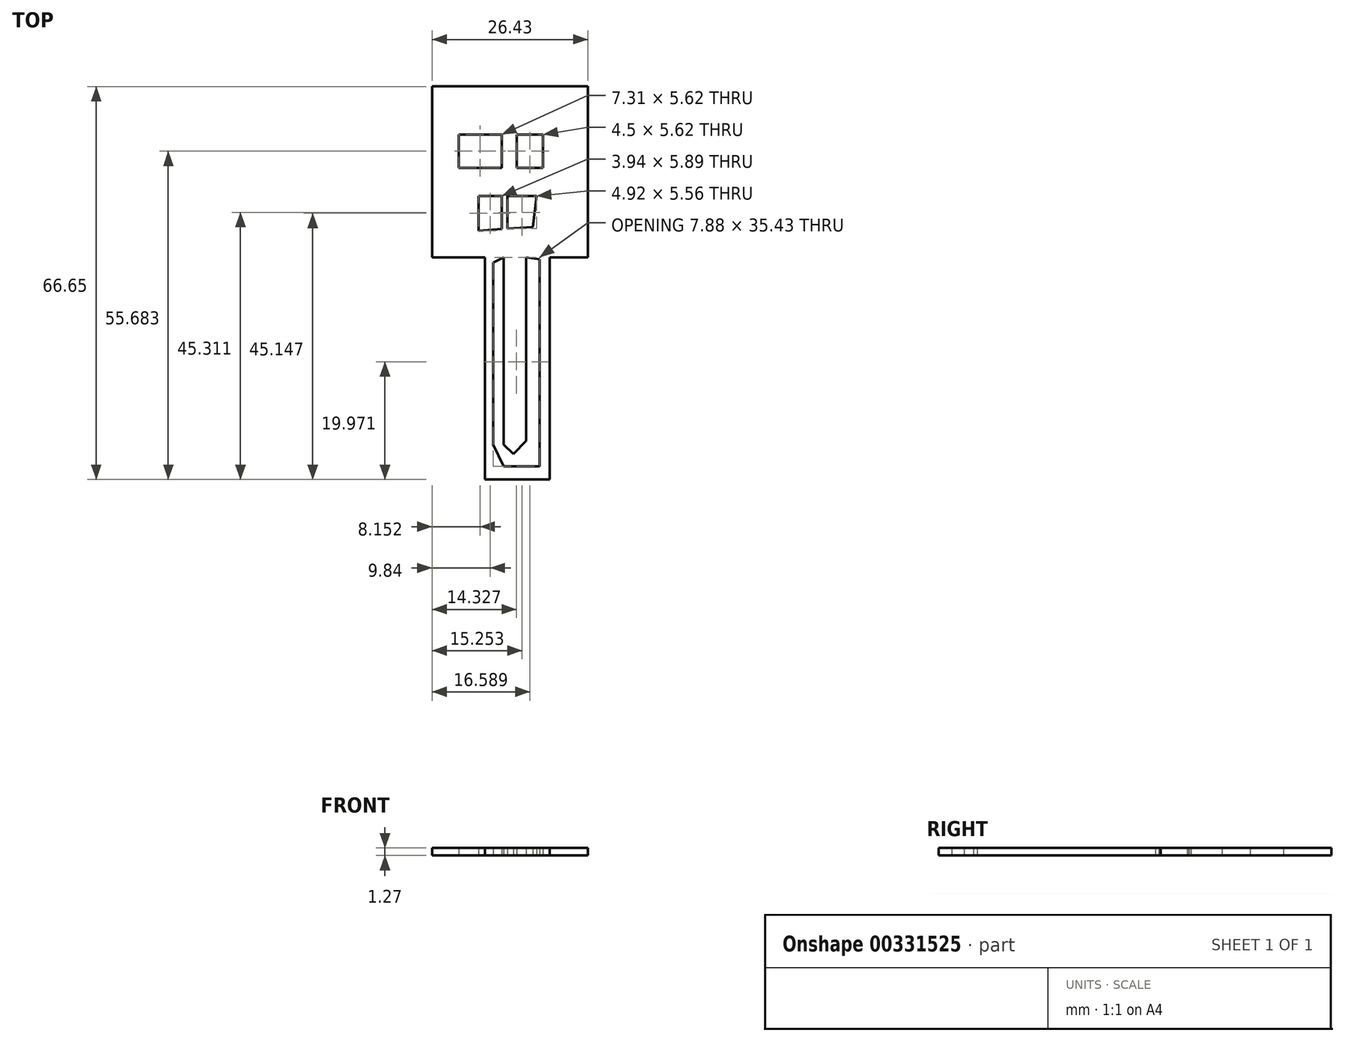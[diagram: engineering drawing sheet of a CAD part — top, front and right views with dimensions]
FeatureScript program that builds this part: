
annotation { "Feature Type Name" : "Feature", "Feature Type Description" : "" }
export const myFeature = defineFeature(function(context is Context, id is Id, definition is map)
    precondition{}
    {
        {
            var Q0;
            Q0=qCreatedBy(makeId("Top.planeOp"),FACE);
            var sketch = newSketch(context, id + "F0", { "sketchPlane" : qUnion([Q0])});
            skLineSegment(sketch, "E0", {"start": v(-60.18, 43.73) * mm, "end": v(-60.18, 14.76) * mm});
            skLineSegment(sketch, "E1", {"start": v(-60.18, 43.73) * mm, "end": v(-33.75, 43.73) * mm});
            skLineSegment(sketch, "E2", {"start": v(-33.75, 43.73) * mm, "end": v(-33.75, 14.76) * mm});
            skLineSegment(sketch, "E3", {"start": v(-33.75, 14.76) * mm, "end": v(-40.22, 14.76) * mm});
            skLineSegment(sketch, "E4", {"start": v(-40.22, 14.76) * mm, "end": v(-40.22, -22.92) * mm});
            skLineSegment(sketch, "E5", {"start": v(-40.22, -22.92) * mm, "end": v(-51.18, -22.92) * mm});
            skLineSegment(sketch, "E6", {"start": v(-51.18, -22.92) * mm, "end": v(-51.18, 14.76) * mm});
            skLineSegment(sketch, "E7", {"start": v(-52.03, 43.73) * mm, "end": v(-52.03, 38.1) * mm});
            skLineSegment(sketch, "E8", {"start": v(-44.72, 43.73) * mm, "end": v(-44.72, 38.1) * mm});
            skLineSegment(sketch, "E9.bottom", {"start": v(-48.37, 29.95) * mm, "end": v(-55.68, 29.95) * mm});
            skLineSegment(sketch, "E9.top", {"start": v(-48.37, 35.58) * mm, "end": v(-55.68, 35.58) * mm});
            skLineSegment(sketch, "E9.left", {"start": v(-48.37, 29.95) * mm, "end": v(-48.37, 35.58) * mm});
            skLineSegment(sketch, "E9.right", {"start": v(-55.68, 29.95) * mm, "end": v(-55.68, 35.58) * mm});
            skPoint(sketch, "E9.middle", {"position": v(-52.03, 32.76) * mm});
            skPoint(sketch, "E9.cornerSnap0", {"position": v(-48.37, 36.42) * mm});
            skLineSegment(sketch, "E10.bottom", {"start": v(-45.84, 29.95) * mm, "end": v(-41.34, 29.95) * mm});
            skLineSegment(sketch, "E10.top", {"start": v(-45.84, 35.58) * mm, "end": v(-41.34, 35.58) * mm});
            skLineSegment(sketch, "E10.left", {"start": v(-45.84, 29.95) * mm, "end": v(-45.84, 35.58) * mm});
            skLineSegment(sketch, "E10.right", {"start": v(-41.34, 29.95) * mm, "end": v(-41.34, 35.58) * mm});
            skPoint(sketch, "E10.middle", {"position": v(-43.6, 32.76) * mm});
            skLineSegment(sketch, "E11", {"start": v(-52.3, 25.17) * mm, "end": v(-52.3, 19.28) * mm});
            skLineSegment(sketch, "E12", {"start": v(-52.3, 19.28) * mm, "end": v(-48.37, 19.55) * mm});
            skLineSegment(sketch, "E13", {"start": v(-52.3, 25.17) * mm, "end": v(-48.37, 25.17) * mm});
            skLineSegment(sketch, "E14", {"start": v(-48.05, 14.76) * mm, "end": v(-48.05, -17.01) * mm});
            skPoint(sketch, "E15.endSnap0", {"position": v(-45.7, -22.92) * mm});
            skLineSegment(sketch, "E16", {"start": v(-41.91, -17.23) * mm, "end": v(-41.63, -17.01) * mm});
            skLineSegment(sketch, "E17", {"start": v(-45.47, 36.42) * mm, "end": v(-45.84, 35.58) * mm});
            skLineSegment(sketch, "E18", {"start": v(-60.18, 14.76) * mm, "end": v(-51.18, 14.76) * mm});
            skLineSegment(sketch, "E19", {"start": v(-42.47, 25.17) * mm, "end": v(-43.09, 19.9) * mm});
            skPoint(sketch, "E20.start.orphan", {"position": v(-47.39, 25.17) * mm});
            skLineSegment(sketch, "E21", {"start": v(-44.72, 38.1) * mm, "end": v(-45.47, 36.42) * mm});
            skPoint(sketch, "E22.startSnap0", {"position": v(-43.6, 35.58) * mm});
            skPoint(sketch, "E22.endSnap0", {"position": v(-48.37, 32.76) * mm});
            skLineSegment(sketch, "E23", {"start": v(-49.8, 13.87) * mm, "end": v(-49.8, 1.66) * mm});
            skLineSegment(sketch, "E24", {"start": v(-49.8, 1.66) * mm, "end": v(-49.8, -10.1) * mm});
            skLineSegment(sketch, "E25", {"start": v(-49.8, -10.1) * mm, "end": v(-49.8, -17.01) * mm});
            skLineSegment(sketch, "E26", {"start": v(-49.8, -17.01) * mm, "end": v(-48.05, -20.66) * mm});
            skLineSegment(sketch, "E27", {"start": v(-48.05, -20.66) * mm, "end": v(-45.7, -20.66) * mm});
            skLineSegment(sketch, "E28", {"start": v(-45.7, -20.66) * mm, "end": v(-41.91, -20.66) * mm});
            skLineSegment(sketch, "E29", {"start": v(-41.91, -20.66) * mm, "end": v(-41.91, -11.02) * mm});
            skLineSegment(sketch, "E30", {"start": v(-41.91, -11.02) * mm, "end": v(-41.91, -2.64) * mm});
            skLineSegment(sketch, "E31", {"start": v(-41.91, -2.64) * mm, "end": v(-41.91, 5.39) * mm});
            skLineSegment(sketch, "E32", {"start": v(-41.91, 5.39) * mm, "end": v(-41.91, 14.46) * mm});
            skPoint(sketch, "E33.start.orphan", {"position": v(-48.37, 19.55) * mm});
            skLineSegment(sketch, "E34", {"start": v(-49.8, 13.87) * mm, "end": v(-48.05, 14.76) * mm});
            skLineSegment(sketch, "E35", {"start": v(-41.91, 14.46) * mm, "end": v(-40.22, 14.76) * mm});
            skPoint(sketch, "E36.start.orphan", {"position": v(-56.8, 36.42) * mm});
            skPoint(sketch, "E37.startSnap0", {"position": v(-36.98, 14.76) * mm});
            skPoint(sketch, "E37.start.orphan", {"position": v(-36.98, 17.85) * mm});
            skPoint(sketch, "E38.trimOffspring.end.orphan", {"position": v(-39.93, 36.42) * mm});
            skLineSegment(sketch, "E39", {"start": v(-52.03, 38.1) * mm, "end": v(-48.37, 35.58) * mm});
            skPoint(sketch, "E40.start.orphan", {"position": v(-42.75, 14.76) * mm});
            skPoint(sketch, "E15.end.orphan", {"position": v(-45.7, -20.1) * mm});
            skLineSegment(sketch, "E41", {"start": v(-48.05, -17.01) * mm, "end": v(-46.4, -18.6) * mm});
            skLineSegment(sketch, "E42", {"start": v(-46.4, -18.6) * mm, "end": v(-44.25, -16.36) * mm});
            skLineSegment(sketch, "E43", {"start": v(-44.25, -16.36) * mm, "end": v(-44.25, 14.76) * mm});
            skLineSegment(sketch, "E44", {"start": v(-44.25, 14.76) * mm, "end": v(-41.91, 14.46) * mm});
            skLineSegment(sketch, "E45", {"start": v(-48.37, 25.17) * mm, "end": v(-48.37, 19.55) * mm});
            skLineSegment(sketch, "E46", {"start": v(-47.39, 25.17) * mm, "end": v(-47.39, 19.55) * mm});
            skLineSegment(sketch, "E47.trimOffspring", {"start": v(-47.39, 19.61) * mm, "end": v(-43.09, 19.9) * mm});
            skLineSegment(sketch, "E48.trimOffspring", {"start": v(-47.39, 25.17) * mm, "end": v(-42.47, 25.17) * mm});
            skSolve(sketch);
        }
        {
            var Q0;
            Q0 = qSketchRegion(id + "F0", true);
            extrude(context, id + "F1", {"entities" : qUnion([Q0]), "depth" : 1.27 * mm});
        }
    });
